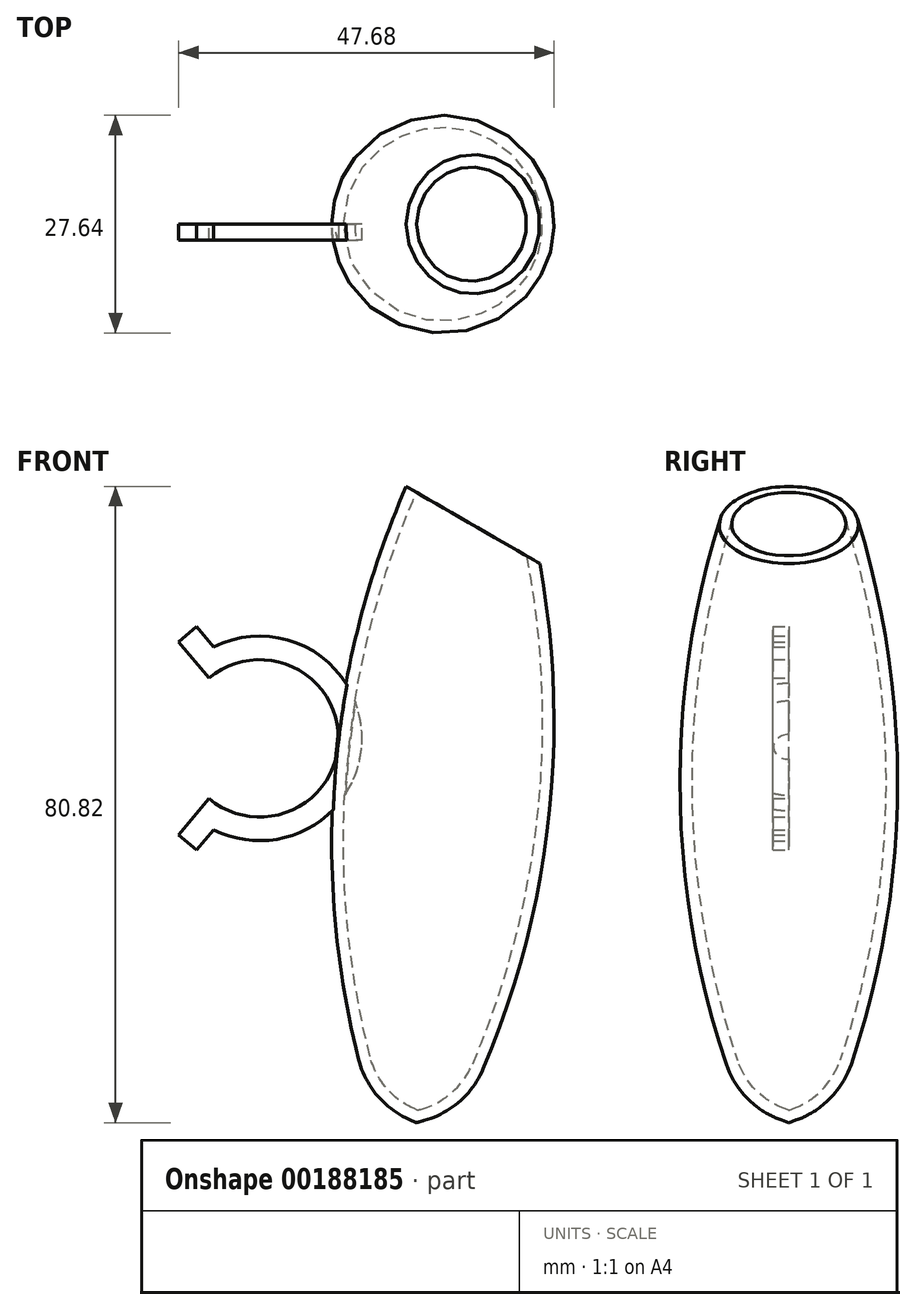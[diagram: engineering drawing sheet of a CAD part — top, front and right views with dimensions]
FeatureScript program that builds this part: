
annotation { "Feature Type Name" : "Feature", "Feature Type Description" : "" }
export const myFeature = defineFeature(function(context is Context, id is Id, definition is map)
    precondition{}
    {
        {
            var Q0;
            Q0=qCreatedBy(makeId("Front.planeOp"),FACE);
            var sketch = newSketch(context, id + "F0", { "sketchPlane" : qUnion([Q0])});
            skArc(sketch, "E0", {"start": v(-47.18, -7.66) * mm, "mid": v(-30.75, 0) * mm, "end": v(-47.18, 7.66) * mm});
            skLineSegment(sketch, "E1", {"start": v(-47.18, 7.66) * mm, "end": v(-51.04, 12.26) * mm});
            skLineSegment(sketch, "E2", {"start": v(-51.04, 12.26) * mm, "end": v(-48.74, 14.19) * mm});
            skLineSegment(sketch, "E3", {"start": v(-48.74, 14.19) * mm, "end": v(-46.58, 11.62) * mm});
            skLineSegment(sketch, "E4.MirrorCS", {"start": v(-48.74, -14.19) * mm, "end": v(-46.58, -11.62) * mm});
            skLineSegment(sketch, "E5.MirrorCS", {"start": v(-47.18, -7.66) * mm, "end": v(-51.04, -12.26) * mm});
            skLineSegment(sketch, "E6.MirrorCS", {"start": v(-51.04, -12.26) * mm, "end": v(-48.74, -14.19) * mm});
            skArc(sketch, "E7.trimOffspring", {"start": v(-46.58, -11.62) * mm, "mid": v(-27.75, 0) * mm, "end": v(-46.58, 11.62) * mm});
            skSolve(sketch);
        }
        {
            var Q0;
            Q0=makeQuery(id+"F0.imprint","IMPRINT",FACE,{"disambiguationData":[TD([[makeQuery(id+"F0.imprint","IMPRINT",EDGE,{"derivedFrom":sQuery(id+"F0.wireOp",EDGE,"E0")}),-1.0]])]});
            extrude(context, id + "F1", {"entities" : qUnion([Q0]), "depth" : 2 * mm});
        }
        {
            var Q0;
            Q0=qCreatedBy(makeId("Front.planeOp"),FACE);
            var sketch = newSketch(context, id + "F2", { "sketchPlane" : qUnion([Q0])});
            skArc(sketch, "E8", {"start": v(-21.23, 34) * mm, "mid": v(-31.12, -2.78) * mm, "end": v(-28.19, -40.75) * mm});
            skArc(sketch, "E9", {"start": v(-28.19, -40.75) * mm, "mid": v(-25.86, -45.31) * mm, "end": v(-21.78, -48.4) * mm});
            skLineSegment(sketch, "E10", {"start": v(-21.78, -48.4) * mm, "end": v(-20.85, -48.82) * mm});
            skLineSegment(sketch, "E11.0", {"start": v(-21.17, -47.03) * mm, "end": v(-20.73, -47.23) * mm});
            skArc(sketch, "E11.1", {"start": v(-26.73, -40.39) * mm, "mid": v(-24.71, -44.35) * mm, "end": v(-21.17, -47.03) * mm});
            skArc(sketch, "E11.2", {"start": v(-20.8, 31.28) * mm, "mid": v(-29.72, -4.06) * mm, "end": v(-26.73, -40.39) * mm});
            skLineSegment(sketch, "E12", {"start": v(-21.23, 34) * mm, "end": v(-20.8, 31.28) * mm});
            skLineSegment(sketch, "E13", {"start": v(-20.85, -48.82) * mm, "end": v(-20.73, -47.23) * mm});
            skSolve(sketch);
        }
        {
            var Q0;
            Q0=qCreatedBy(makeId("Front.planeOp"),FACE);
            var sketch = newSketch(context, id + "F3", { "sketchPlane" : qUnion([Q0])});
            skLineSegment(sketch, "E14", {"start": v(-21.17, -52.96) * mm, "end": v(-13.72, 42.67) * mm, "construction": true});
            skSolve(sketch);
        }
        {
            var Q0;
            Q0 = qSketchRegion(id + "F2", true);
            var Q1;
            Q1=sQuery(id+"F3.wireOp",EDGE,"E14");
            revolve(context, id + "F4", {"operationType" : NewBodyOperationType.ADD, "entities" : qUnion([Q0]), "axis" : qUnion([Q1]), "revolveType" : RevolveType.FULL});
        }
        {
            var Q0;
            Q0=qCreatedBy(makeId("Front.planeOp"),FACE);
            var sketch = newSketch(context, id + "F5", { "sketchPlane" : qUnion([Q0])});
            skLineSegment(sketch, "E15", {"start": v(-40.22, 42.44) * mm, "end": v(38.37, -2.93) * mm});
            skLineSegment(sketch, "E16", {"start": v(-40.22, 42.44) * mm, "end": v(-33.65, 53.82) * mm});
            skLineSegment(sketch, "E17", {"start": v(-33.65, 53.82) * mm, "end": v(48.86, 4.35) * mm});
            skLineSegment(sketch, "E18", {"start": v(48.86, 4.35) * mm, "end": v(38.37, -2.93) * mm});
            skSolve(sketch);
        }
        {
            var Q0;
            Q0 = qSketchRegion(id + "F5", true);
            extrude(context, id + "F6", {"entities" : qUnion([Q0]), "operationType" : NewBodyOperationType.REMOVE, "endBound" : BoundingType.SYMMETRIC, "oppositeDirection" : true, "depth" : 25 * mm});
        }
    });
